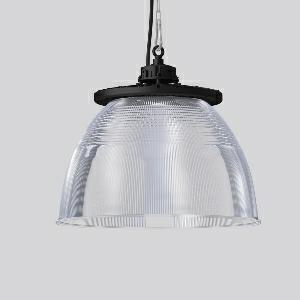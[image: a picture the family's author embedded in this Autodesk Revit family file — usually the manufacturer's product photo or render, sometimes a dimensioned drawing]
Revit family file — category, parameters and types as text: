
# Revit family: industrial_hall_refraktor_921704_003_76_3c25
name_source: partatom
category: Lighting Fixtures
units: mm (PartAtom-declared; Revit-internal decimal feet)

## family parameters
Cut with Voids When Loaded = No
Host = Face
Light Source = No
Part Type = Normal
Room Calculation Point = No
Round Connector Dimension = Use Diameter
Shared = No

## types (1)
- INDUSTRIAL HALL refraktor (1 x LED Modul 840, 11700 lm, 4000)
    Apparent Load = 85 VA
    CIE Flux Codes = 88 97 99 94 100
    Color Rendering = 80
    Color Temperature = 4000
    Default Elevation = 1800 mm
    Description = Series: INDUSTRIAL HALL
Round highbay luminaire for chain or cable suspension. Robust housing made of die-cast aluminium with eye ring, powder coated. Vertical cooling ribs ensure constant heat dissipation for optimal thermal management. Diffuser made of clear, non-reflecting, single pane safety glass (toughened glass). Refractor: PMMA, transparent. Primary light control with high-performance wide-area LEDs and reflector made of plastic (PMMA) for optimum glare limitation: RUG <19. Easy to install thanks to 1-point suspension. Suitable for chain or steel cable suspension (to be provided on site). With power cord (1.5 m). Dimming range 10% to 100%. Ceiling- and wall-mounting bracket available as accessory. Luminaire with limited surface temperature in accordance with EN 60598-2-24 for use in environments in which a deposit of conductive dust on the luminaire can be expected. Qualified for use in the food and drink industry. 
Colour: deep black, matt (RAL 9005)
Diameter: 570 mm
Height: 509 mm
Lamp: LED
Socket: without socket
Colour temperature: 4000K
Colour rendering index (CRI): 80
System power: 85 W
Rated luminous flux: 11700 lm
Luminous efficiency: 138 lm/W
Control gear: Converter, dimmable, DALI
Protection class: I
Type of protection: IP 65
    Height = 509 mm
    Lamp = 1 x LED Modul 840
    Lamp Light Flux = 11700 lm
    Lamp count = 1
    Length = 570 mm
    Lifetime = 50000 h
    Luminous efficacy = 138 lm/W
    Manufacturer = RZB
    ModVariant = No
    Model = 921704.003.76
    Mounting Place = Ceiling
    Mounting Type = Pendant
    Number of Poles = 1
    OnlyDefault = Yes
    Power Factor = 1
    Product Name = INDUSTRIAL HALL refraktor
    Product group = Pendant commercial luminaires
    ProductGroupID = 903
    Protection Class = Protection class I
    Protection Degree = Degree of protection
    RLX_Detail_Level = 1
    RLX_Emergency_Light_Flux = 0 lm
    RLX_Emergency_Type = 0
    RLX_Emergency_Type_DB = No
    RlxData = <blob elided: 253733 chars, md5=369e35c7>
    Socket = socket
    Standby Power = 0 W
    System Light Flux = 11700 lm
    System Power = 85 W
    Type Comments = Product without accessories
    Type Image = 921704.003.jpg
    URL = http://relux.com
    VarID = ---
    Voltage = 0 V
    Weight = 0.00 kg
    Width = 0 mm  [stored 0 ft]

note: [stored X ft] marks values corroborated as IEEE doubles in the binary element streams (Revit-internal decimal feet)

## geometry (parser evidence)
native form markers: Blend x4, Sweep x12
no freeform markers — native parametric forms only
